# Revit family: 28L 4 to 12 units back to back outdoor manifold system
name_source: partatom
category: Plumbing Fixtures
revit_build: Autodesk Revit LT 2017 (Build: 20160225_1515(x64)
units: mm (PartAtom-declared; Revit-internal decimal feet)

## family parameters
Always vertical = Yes
Cut with Voids When Loaded = No
Part Type = Normal
Room Calculation Point = No
Round Connector Dimension = Use Diameter
Shared = No
Work Plane-Based = No

## types (5) — shared parameters
Base Support L = Yes
Base Support R = Yes
Cold Water Inlet Pipe connector description = Male threaded connector R1-1/2"
Cold Water Inlet Pipe diameter = 38.1mm(DN 40)
Gas Inlet Pipe connector description = Male threaded connector R1-1/2"
Gas Inlet Pipe diameter = 38.1mm(DN 40)
Hot Water Outlet Pipe connector description = Male threaded connector R1-1/2"
Hot Water Outlet Pipe diameter = 38.1mm(DN 40)
Nominal depth = 900mm
Nominal height = 1540mm

## per-type parameters (varying)
| type | 2 Unit L | 2 Unit R | 3 Unit L | 3 Unit R | Base Offset L | Base Offset R | Centre | No. of power supply point required | Nominal width | Number of Gas Water Heaters | Product SKU Dux brand | Product SKU Thermann brand | Product description | Total Max. power requirement | Total nominal gas consumption (MJ/h) | Weight (Kg) |
| 28L 4 units Back to back outdoor | Yes | No | No | No | 794 mm | 0 mm | No | 4 | 794 | 4 | D42800EN/LBx | T42800EN/LBx | Gas Water heater Manifold 4 units outdoor back to back | 772W | 880 | 180 |
| 28L 6 units Back to back outdoor | No | No | Yes | No | 1170 mm | 0 mm | No | 6 | 1170mm | 6 | D62800EN/LBx | T62800EN/LBx | Gas Water heater Manifold 6 units outdoor back to back | 1158W | 1230 | 240 |
| 28L 8 units Back to back outdoor | Yes | Yes | No | No | 794 mm | 794 mm | Yes | 8 | 1588mm | 8 | D82800EN/LBx | T82800EN/LBx | Gas Water heater Manifold 8 units outdoor back to back | 1556W | 1640 | 360 |
| 28L 10 units Back to back outdoor | No | Yes | Yes | No | 1170 mm | 794 mm | Yes | 10 | 1964mm | 10 | D102800EN/LBx | T102800EN/LBx | Gas Water heater Manifold 10 units outdoor back to back | 1942 | 2050 | 420 |
| 28L 12 units Back to back outdoor | No | No | Yes | Yes | 1170 mm | 1170 mm | Yes | 12 | 2340mm | 12 | D122800EN/LBx | T122800EN/LBx | Gas Water heater Manifold 12 units outdoor back to back | 2328 | 2460 | 480 |

## geometry (parser evidence)
native form markers: Sweep x14
no freeform markers — native parametric forms only
